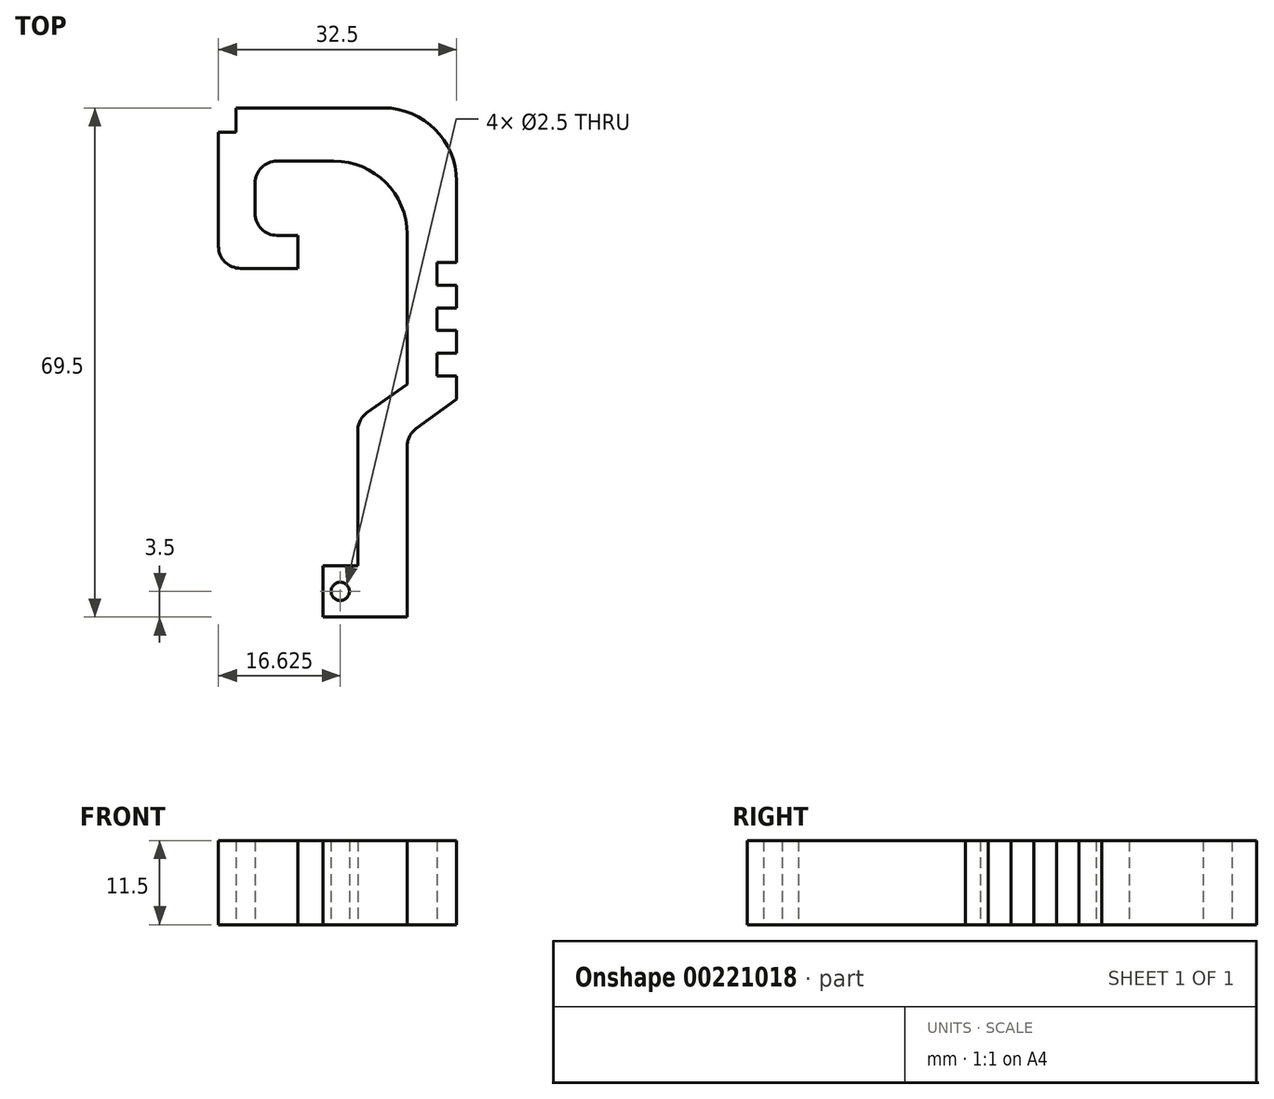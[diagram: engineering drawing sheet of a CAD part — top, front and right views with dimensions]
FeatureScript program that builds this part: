
annotation { "Feature Type Name" : "Feature", "Feature Type Description" : "" }
export const myFeature = defineFeature(function(context is Context, id is Id, definition is map)
    precondition{}
    {
        {
            var Q0;
            Q0=qCreatedBy(makeId("Top.planeOp"),FACE);
            var sketch = newSketch(context, id + "F0", { "sketchPlane" : qUnion([Q0])});
            skLineSegment(sketch, "E0.bottom", {"start": v(4.75, -34.75) * mm, "end": v(9.5, -34.75) * mm});
            skLineSegment(sketch, "E0.top", {"start": v(-13.84, 34.75) * mm, "end": v(6.25, 34.75) * mm});
            skLineSegment(sketch, "E0.left", {"start": v(-16.25, 15.85) * mm, "end": v(-16.25, 31.44) * mm});
            skPoint(sketch, "E0.middle", {"position": v(0, 0) * mm});
            skLineSegment(sketch, "E1", {"start": v(-8.25, 27.5) * mm, "end": v(-0.5, 27.5) * mm});
            skLineSegment(sketch, "E2", {"start": v(9.5, 17.5) * mm, "end": v(9.5, -2.96) * mm});
            skLineSegment(sketch, "E3", {"start": v(-13.25, 12.85) * mm, "end": v(-5.43, 12.85) * mm});
            skLineSegment(sketch, "E4", {"start": v(-5.43, 12.85) * mm, "end": v(-5.43, 17.35) * mm});
            skLineSegment(sketch, "E5", {"start": v(-5.43, 17.35) * mm, "end": v(-8.25, 17.35) * mm});
            skLineSegment(sketch, "E6", {"start": v(-11.25, 20.35) * mm, "end": v(-11.25, 24.5) * mm});
            skPoint(sketch, "E7.visualSharp", {"position": v(-11.25, 17.35) * mm});
            skArc(sketch, "E7.filletArc", {"start": v(-11.25, 20.35) * mm, "mid": v(-10.37, 18.23) * mm, "end": v(-8.25, 17.35) * mm});
            skPoint(sketch, "E8.visualSharp", {"position": v(-11.25, 27.5) * mm});
            skArc(sketch, "E8.filletArc", {"start": v(-8.25, 27.5) * mm, "mid": v(-10.37, 26.62) * mm, "end": v(-11.25, 24.5) * mm});
            skPoint(sketch, "E9.visualSharp", {"position": v(9.5, 27.5) * mm});
            skArc(sketch, "E9.filletArc", {"start": v(9.5, 17.5) * mm, "mid": v(6.57, 24.57) * mm, "end": v(-0.5, 27.5) * mm});
            skPoint(sketch, "E10.visualSharp", {"position": v(16.25, 34.75) * mm});
            skArc(sketch, "E10.filletArc", {"start": v(16.25, 24.75) * mm, "mid": v(13.32, 31.82) * mm, "end": v(6.25, 34.75) * mm});
            skPoint(sketch, "E11.orphan", {"position": v(-16.25, -34.75) * mm});
            skPoint(sketch, "E12.visualSharp", {"position": v(-16.25, 12.85) * mm});
            skArc(sketch, "E12.filletArc", {"start": v(-16.25, 15.85) * mm, "mid": v(-15.37, 13.73) * mm, "end": v(-13.25, 12.85) * mm});
            skLineSegment(sketch, "E13", {"start": v(-16.25, 31.44) * mm, "end": v(-13.84, 31.44) * mm});
            skLineSegment(sketch, "E14", {"start": v(-13.84, 31.44) * mm, "end": v(-13.84, 34.75) * mm});
            skPoint(sketch, "E15.orphan", {"position": v(-16.25, 34.75) * mm});
            skLineSegment(sketch, "E16", {"start": v(4, 16.75) * mm, "end": v(16.25, 16.75) * mm, "construction": true});
            skLineSegment(sketch, "E17", {"start": v(16.25, 13.65) * mm, "end": v(13.6, 13.65) * mm});
            skLineSegment(sketch, "E18", {"start": v(13.6, 13.65) * mm, "end": v(13.6, 10.55) * mm});
            skLineSegment(sketch, "E19", {"start": v(13.6, 10.55) * mm, "end": v(16.25, 10.55) * mm});
            skLineSegment(sketch, "E20", {"start": v(16.25, 7.45) * mm, "end": v(13.6, 7.45) * mm});
            skLineSegment(sketch, "E21", {"start": v(13.6, 7.45) * mm, "end": v(13.6, 4.35) * mm});
            skLineSegment(sketch, "E22", {"start": v(13.6, 4.35) * mm, "end": v(16.25, 4.35) * mm});
            skLineSegment(sketch, "E23", {"start": v(16.25, 1.25) * mm, "end": v(13.6, 1.25) * mm});
            skLineSegment(sketch, "E24", {"start": v(13.6, 1.25) * mm, "end": v(13.6, -1.85) * mm});
            skLineSegment(sketch, "E25", {"start": v(13.6, -1.85) * mm, "end": v(16.25, -1.85) * mm});
            skLineSegment(sketch, "E26", {"start": v(16.25, -5) * mm, "end": v(10.73, -9.04) * mm});
            skLineSegment(sketch, "E27", {"start": v(2.75, -9.94) * mm, "end": v(2.75, -27.75) * mm});
            skLineSegment(sketch, "E28", {"start": v(2.75, -27.75) * mm, "end": v(-2, -27.75) * mm});
            skLineSegment(sketch, "E29", {"start": v(-2, -27.75) * mm, "end": v(-2, -34.75) * mm});
            skLineSegment(sketch, "E30", {"start": v(-2, -34.75) * mm, "end": v(4.75, -34.75) * mm});
            skLineSegment(sketch, "E31", {"start": v(9.5, -27.75) * mm, "end": v(9.5, -34.75) * mm});
            skLineSegment(sketch, "E32.trimOffspring", {"start": v(16.25, -5) * mm, "end": v(16.25, -1.85) * mm});
            skPoint(sketch, "E33.orphan", {"position": v(16.25, -34.75) * mm});
            skPoint(sketch, "E34.end.orphan", {"position": v(4.75, -27.75) * mm});
            skLineSegment(sketch, "E35", {"start": v(9.5, -2.96) * mm, "end": v(4, -6.88) * mm});
            skLineSegment(sketch, "E36", {"start": v(2.75, -9.32) * mm, "end": v(2.75, -9.94) * mm});
            skPoint(sketch, "E37.start.orphan", {"position": v(9.5, -5.13) * mm});
            skLineSegment(sketch, "E38.trimOffspring", {"start": v(9.5, -11.46) * mm, "end": v(9.5, -27.75) * mm});
            skLineSegment(sketch, "E39.trimOffspring", {"start": v(16.25, 1.25) * mm, "end": v(16.25, 4.35) * mm});
            skLineSegment(sketch, "E40.trimOffspring", {"start": v(16.25, 7.45) * mm, "end": v(16.25, 10.55) * mm});
            skLineSegment(sketch, "E41.trimOffspring", {"start": v(16.25, 13.65) * mm, "end": v(16.25, 24.75) * mm});
            skPoint(sketch, "E42.visualSharp", {"position": v(2.75, -7.78) * mm});
            skArc(sketch, "E42.filletArc", {"start": v(4, -6.88) * mm, "mid": v(3.08, -7.95) * mm, "end": v(2.75, -9.32) * mm});
            skPoint(sketch, "E43.visualSharp", {"position": v(9.5, -9.94) * mm});
            skArc(sketch, "E43.filletArc", {"start": v(10.73, -9.04) * mm, "mid": v(9.82, -10.1) * mm, "end": v(9.5, -11.46) * mm});
            skLineSegment(sketch, "E44", {"start": v(-2, -31.25) * mm, "end": v(9.5, -31.25) * mm, "construction": true});
            skLineSegment(sketch, "E45", {"start": v(9.5, -31.25) * mm, "end": v(9.2, -31.13) * mm, "construction": true});
            skLineSegment(sketch, "E46", {"start": v(0.38, -27.75) * mm, "end": v(0.38, -34.75) * mm, "construction": true});
            skCircle(sketch, "E47", {"center": v(0.38, -31.25) * mm, "radius": 1.25 * mm});
            skSolve(sketch);
        }
        {
            var Q0;
            Q0=makeQuery(id+"F0.imprint","IMPRINT",FACE,{"disambiguationData":[TD([[makeQuery(id+"F0.imprint","IMPRINT",EDGE,{"derivedFrom":sQuery(id+"F0.wireOp",EDGE,"E0.bottom")}),1.0]])]});
            extrude(context, id + "F1", {"entities" : qUnion([Q0]), "depth" : 11.5 * mm});
        }
    });
